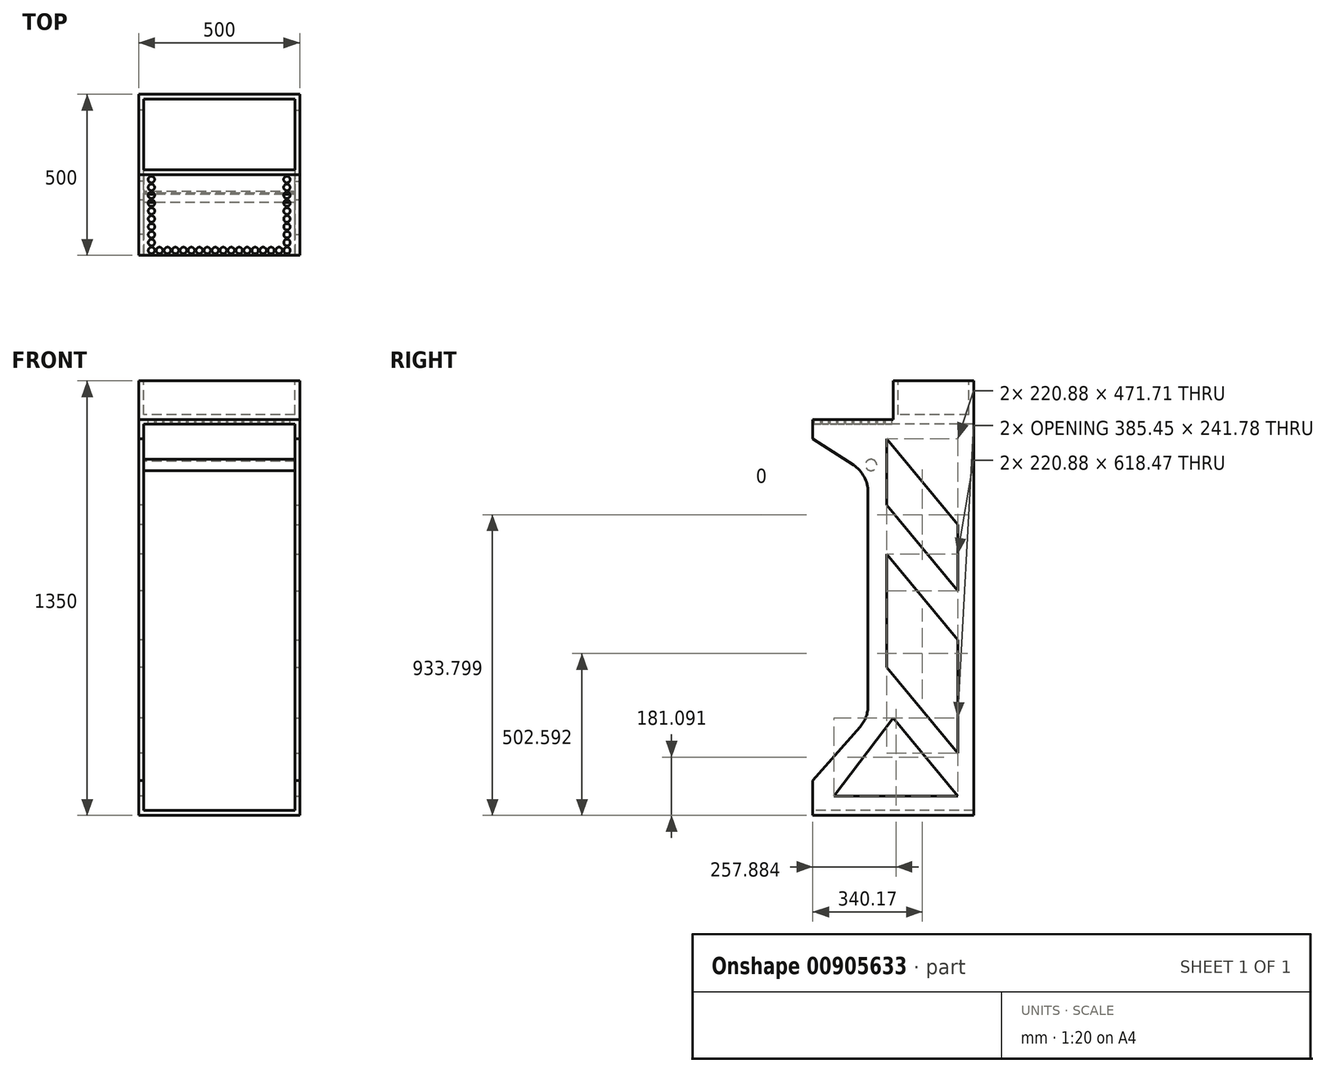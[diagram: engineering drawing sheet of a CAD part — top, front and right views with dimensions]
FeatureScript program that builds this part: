
annotation { "Feature Type Name" : "Feature", "Feature Type Description" : "" }
export const myFeature = defineFeature(function(context is Context, id is Id, definition is map)
    precondition{}
    {
        {
            var Q0;
            Q0=qCreatedBy(makeId("Top.planeOp"),FACE);
            var sketch = newSketch(context, id + "F0", { "sketchPlane" : qUnion([Q0])});
            skLineSegment(sketch, "E0.bottom", {"start": v(250, 250) * mm, "end": v(-250, 250) * mm});
            skLineSegment(sketch, "E0.top", {"start": v(250, -250) * mm, "end": v(-250, -250) * mm});
            skLineSegment(sketch, "E0.left", {"start": v(250, 250) * mm, "end": v(250, -250) * mm});
            skLineSegment(sketch, "E0.right", {"start": v(-250, 250) * mm, "end": v(-250, -250) * mm});
            skPoint(sketch, "E0.middle", {"position": v(0, 0) * mm});
            skSolve(sketch);
        }
        {
            var Q0;
            Q0 = qSketchRegion(id + "F0", true);
            extrude(context, id + "F1", {"entities" : qUnion([Q0]), "depth" : 15 * mm, "offsetDistance" : 25 * mm});
        }
        {
            var Q0;
            Q0=makeQuery(id+"F1.opExtrude","CAP_FACE",FACE,{"disambiguationData":[OSD([sQuery(id+"F0.wireOp",EDGE,"E0.bottom"),sQuery(id+"F0.wireOp",EDGE,"E0.top"),sQuery(id+"F0.wireOp",EDGE,"E0.left"),sQuery(id+"F0.wireOp",EDGE,"E0.right")])],"isStart":false});
            var sketch = newSketch(context, id + "F2", { "sketchPlane" : qUnion([Q0])});
            skLineSegment(sketch, "E1.bottom", {"start": v(-250, 250) * mm, "end": v(-235, 250) * mm});
            skLineSegment(sketch, "E1.top", {"start": v(-250, -250) * mm, "end": v(-235, -250) * mm});
            skLineSegment(sketch, "E1.left", {"start": v(-250, 250) * mm, "end": v(-250, -250) * mm});
            skLineSegment(sketch, "E1.right", {"start": v(-235, 250) * mm, "end": v(-235, -250) * mm});
            skLineSegment(sketch, "E2.bottom", {"start": v(250, 250) * mm, "end": v(235, 250) * mm});
            skLineSegment(sketch, "E2.top", {"start": v(250, -250) * mm, "end": v(235, -250) * mm});
            skLineSegment(sketch, "E2.left", {"start": v(250, 250) * mm, "end": v(250, -250) * mm});
            skLineSegment(sketch, "E2.right", {"start": v(235, 250) * mm, "end": v(235, -250) * mm});
            skSolve(sketch);
        }
        {
            var Q0;
            Q0=makeQuery(id+"F2.imprint","IMPRINT",FACE,{"disambiguationData":[TD([[makeQuery(id+"F2.imprint","IMPRINT",EDGE,{"derivedFrom":sQuery(id+"F2.wireOp",EDGE,"E1.bottom")}),1.0]])]});
            var Q1;
            Q1=makeQuery(id+"F2.imprint","IMPRINT",FACE,{"disambiguationData":[TD([[makeQuery(id+"F2.imprint","IMPRINT",EDGE,{"derivedFrom":sQuery(id+"F2.wireOp",EDGE,"E2.bottom")}),1.0]])]});
            extrude(context, id + "F3", {"entities" : qUnion([Q0, Q1]), "operationType" : NewBodyOperationType.ADD, "depth" : 1200 * mm, "offsetDistance" : 25 * mm});
        }
        {
            var Q0;
            Q0=makeQuery(id+"F3.boolean.opBoolean","MERGE",FACE,{"derivedFrom":[makeQuery(id+"F1.opExtrude","SWEPT_FACE",FACE,{"disambiguationData":[OSD([sQuery(id+"F0.wireOp",EDGE,"E0.right")])]}),makeQuery(id+"F3.opExtrude","SWEPT_FACE",FACE,{"disambiguationData":[OSD([sQuery(id+"F2.wireOp",EDGE,"E1.left")])]})]});
            var sketch = newSketch(context, id + "F4", { "sketchPlane" : qUnion([Q0])});
            skLineSegment(sketch, "E3", {"start": v(250, 1169.65) * mm, "end": v(124.16, 1088.19) * mm});
            skLineSegment(sketch, "E4", {"start": v(78.51, 1004.24) * mm, "end": v(78.51, 341.11) * mm});
            skLineSegment(sketch, "E5", {"start": v(103.4, 275.1) * mm, "end": v(250, 108.32) * mm});
            skPoint(sketch, "E6.visualSharp", {"position": v(78.51, 303.4) * mm});
            skArc(sketch, "E6.filletArc", {"start": v(78.51, 341.11) * mm, "mid": v(84.94, 305.83) * mm, "end": v(103.4, 275.1) * mm});
            skPoint(sketch, "E7.visualSharp", {"position": v(78.51, 1058.63) * mm});
            skArc(sketch, "E7.filletArc", {"start": v(124.16, 1088.19) * mm, "mid": v(90.66, 1052.02) * mm, "end": v(78.51, 1004.24) * mm});
            skSolve(sketch);
        }
        {
            var Q0;
            Q0 = qSketchRegion(id + "F4", true);
            var Q1;
            {var subQ1=sQuery(id+"F4.wireOp",EDGE,"E3");Q1=makeQuery(id+"F4.imprint","IMPRINT",FACE,{"disambiguationData":[TD([[makeQuery(id+"F4.imprint","IMPRINT",EDGE,{"derivedFrom":subQ1}),1.0]])]});}
            extrude(context, id + "F5", {"entities" : qUnion([Q0, Q1]), "operationType" : NewBodyOperationType.REMOVE, "oppositeDirection" : true, "depth" : 500 * mm, "offsetDistance" : 25 * mm});
        }
        {
            var Q0;
            Q0=makeQuery(id+"F3.opExtrude","CAP_FACE",FACE,{"disambiguationData":[OSD([sQuery(id+"F2.wireOp",EDGE,"E1.bottom"),sQuery(id+"F2.wireOp",EDGE,"E1.top"),sQuery(id+"F2.wireOp",EDGE,"E1.left"),sQuery(id+"F2.wireOp",EDGE,"E1.right")])],"isStart":false});
            var sketch = newSketch(context, id + "F6", { "sketchPlane" : qUnion([Q0])});
            skLineSegment(sketch, "E8.bottom", {"start": v(-250, 250) * mm, "end": v(250, 250) * mm});
            skLineSegment(sketch, "E8.top", {"start": v(-250, -250) * mm, "end": v(250, -250) * mm});
            skLineSegment(sketch, "E8.left", {"start": v(-250, 250) * mm, "end": v(-250, -250) * mm});
            skLineSegment(sketch, "E8.right", {"start": v(250, 250) * mm, "end": v(250, -250) * mm});
            skSolve(sketch);
        }
        {
            var Q0;
            Q0 = qSketchRegion(id + "F6", true);
            extrude(context, id + "F7", {"entities" : qUnion([Q0]), "operationType" : NewBodyOperationType.ADD, "depth" : 15 * mm, "offsetDistance" : 25 * mm});
        }
        {
            var Q0;
            Q0=makeQuery(id+"F7.opExtrude","CAP_FACE",FACE,{"disambiguationData":[OSD([sQuery(id+"F6.wireOp",EDGE,"E8.bottom"),sQuery(id+"F6.wireOp",EDGE,"E8.top"),sQuery(id+"F6.wireOp",EDGE,"E8.left"),sQuery(id+"F6.wireOp",EDGE,"E8.right")])],"isStart":false});
            var sketch = newSketch(context, id + "F8", { "sketchPlane" : qUnion([Q0])});
            skLineSegment(sketch, "E9", {"start": v(-250, 0) * mm, "end": v(250, 0) * mm});
            skLineSegment(sketch, "E10", {"start": v(250, 0) * mm, "end": v(250, 250) * mm});
            skLineSegment(sketch, "E11", {"start": v(250, 250) * mm, "end": v(-250, 250) * mm});
            skLineSegment(sketch, "E12", {"start": v(-250, 250) * mm, "end": v(-250, 0) * mm});
            skSolve(sketch);
        }
        {
            var Q0;
            Q0=makeQuery(id+"F8.imprint","IMPRINT",FACE,{"disambiguationData":[TD([[makeQuery(id+"F8.imprint","IMPRINT",EDGE,{"derivedFrom":sQuery(id+"F8.wireOp",EDGE,"E9")}),1.0]])]});
            extrude(context, id + "F9", {"entities" : qUnion([Q0]), "operationType" : NewBodyOperationType.ADD, "depth" : 120 * mm, "offsetDistance" : 25 * mm});
        }
        {
            var Q0;
            Q0=makeQuery(id+"F9.opExtrude","CAP_FACE",FACE,{"disambiguationData":[OSD([sQuery(id+"F8.wireOp",EDGE,"E9"),sQuery(id+"F8.wireOp",EDGE,"E10"),sQuery(id+"F8.wireOp",EDGE,"E11"),sQuery(id+"F8.wireOp",EDGE,"E12")])],"isStart":false});
            var sketch = newSketch(context, id + "F10", { "sketchPlane" : qUnion([Q0])});
            skLineSegment(sketch, "E13.0", {"start": v(-235, 235) * mm, "end": v(-235, 15) * mm});
            skLineSegment(sketch, "E13.1", {"start": v(235, 235) * mm, "end": v(-235, 235) * mm});
            skLineSegment(sketch, "E13.2", {"start": v(235, 15) * mm, "end": v(235, 235) * mm});
            skLineSegment(sketch, "E13.3", {"start": v(-235, 15) * mm, "end": v(235, 15) * mm});
            skSolve(sketch);
        }
        {
            var Q0;
            Q0=makeQuery(id+"F10.imprint","IMPRINT",FACE,{"disambiguationData":[TD([[makeQuery(id+"F10.imprint","IMPRINT",EDGE,{"derivedFrom":sQuery(id+"F10.wireOp",EDGE,"E13.0")}),1.0]])]});
            extrude(context, id + "F11", {"entities" : qUnion([Q0]), "operationType" : NewBodyOperationType.REMOVE, "oppositeDirection" : true, "depth" : 105 * mm, "offsetDistance" : 25 * mm});
        }
        {
            var Q0;
            Q0=makeQuery(id+"F7.opExtrude","CAP_FACE",FACE,{"disambiguationData":[OSD([sQuery(id+"F6.wireOp",EDGE,"E8.bottom"),sQuery(id+"F6.wireOp",EDGE,"E8.top"),sQuery(id+"F6.wireOp",EDGE,"E8.left"),sQuery(id+"F6.wireOp",EDGE,"E8.right")])],"isStart":false});
            var sketch = newSketch(context, id + "F12", { "sketchPlane" : qUnion([Q0])});
            skLineSegment(sketch, "E14", {"start": v(235, -250) * mm, "end": v(235, -235) * mm, "construction": true});
            skLineSegment(sketch, "E15", {"start": v(235, -235) * mm, "end": v(250, -235) * mm, "construction": true});
            skCircle(sketch, "E16.1.0.0", {"center": v(-210.25, -235) * mm, "radius": 10 * mm});
            skCircle(sketch, "E16.2.0.0", {"center": v(-185.5, -235) * mm, "radius": 10 * mm});
            skCircle(sketch, "E16.3.0.0", {"center": v(-160.75, -235) * mm, "radius": 10 * mm});
            skCircle(sketch, "E16.4.0.0", {"center": v(-136, -235) * mm, "radius": 10 * mm});
            skCircle(sketch, "E16.5.0.0", {"center": v(-111.25, -235) * mm, "radius": 10 * mm});
            skCircle(sketch, "E16.6.0.0", {"center": v(-86.5, -235) * mm, "radius": 10 * mm});
            skCircle(sketch, "E16.7.0.0", {"center": v(-61.75, -235) * mm, "radius": 10 * mm});
            skCircle(sketch, "E16.8.0.0", {"center": v(-37, -235) * mm, "radius": 10 * mm});
            skCircle(sketch, "E16.9.0.0", {"center": v(-12.25, -235) * mm, "radius": 10 * mm});
            skCircle(sketch, "E16.10.0.0", {"center": v(12.5, -235) * mm, "radius": 10 * mm});
            skCircle(sketch, "E16.11.0.0", {"center": v(37.25, -235) * mm, "radius": 10 * mm});
            skCircle(sketch, "E16.12.0.0", {"center": v(62, -235) * mm, "radius": 10 * mm});
            skCircle(sketch, "E16.13.0.0", {"center": v(86.75, -235) * mm, "radius": 10 * mm});
            skCircle(sketch, "E16.14.0.0", {"center": v(111.5, -235) * mm, "radius": 10 * mm});
            skCircle(sketch, "E16.15.0.0", {"center": v(136.25, -235) * mm, "radius": 10 * mm});
            skCircle(sketch, "E16.16.0.0", {"center": v(161, -235) * mm, "radius": 10 * mm});
            skCircle(sketch, "E16.17.0.0", {"center": v(185.75, -235) * mm, "radius": 10 * mm});
            skCircle(sketch, "E16.18.0.0", {"center": v(210.5, -235) * mm, "radius": 10 * mm});
            skLineSegment(sketch, "E17", {"start": v(235, -250) * mm, "end": v(235, 0) * mm, "construction": true});
            skLineSegment(sketch, "E18", {"start": v(250, -15) * mm, "end": v(235, -15) * mm, "construction": true});
            skLineSegment(sketch, "E19.direction1", {"start": v(235.25, -235) * mm, "end": v(260.25, -235) * mm, "construction": true});
            skCircle(sketch, "E20.0.1.0", {"center": v(-210.3, -210.5) * mm, "radius": 10 * mm});
            skCircle(sketch, "E20.0.2.0", {"center": v(-210.34, -186) * mm, "radius": 10 * mm});
            skCircle(sketch, "E20.0.3.0", {"center": v(-210.39, -161.5) * mm, "radius": 10 * mm});
            skCircle(sketch, "E20.0.4.0", {"center": v(-210.43, -137) * mm, "radius": 10 * mm});
            skCircle(sketch, "E20.0.5.0", {"center": v(-210.48, -112.5) * mm, "radius": 10 * mm});
            skCircle(sketch, "E20.0.6.0", {"center": v(-210.53, -88) * mm, "radius": 10 * mm});
            skCircle(sketch, "E20.0.7.0", {"center": v(-210.57, -63.5) * mm, "radius": 10 * mm});
            skCircle(sketch, "E20.0.8.0", {"center": v(-210.62, -39) * mm, "radius": 10 * mm});
            skCircle(sketch, "E20.0.9.0", {"center": v(-210.66, -14.5) * mm, "radius": 10 * mm});
            skLineSegment(sketch, "E20.direction2", {"start": v(-210.25, -235) * mm, "end": v(-210.3, -210.5) * mm, "construction": true});
            skCircle(sketch, "E21.0.1.0", {"center": v(210.45, -210.5) * mm, "radius": 10 * mm});
            skCircle(sketch, "E21.0.2.0", {"center": v(210.4, -186) * mm, "radius": 10 * mm});
            skCircle(sketch, "E21.0.3.0", {"center": v(210.36, -161.5) * mm, "radius": 10 * mm});
            skCircle(sketch, "E21.0.4.0", {"center": v(210.32, -137) * mm, "radius": 10 * mm});
            skCircle(sketch, "E21.0.5.0", {"center": v(210.27, -112.5) * mm, "radius": 10 * mm});
            skCircle(sketch, "E21.0.6.0", {"center": v(210.22, -88) * mm, "radius": 10 * mm});
            skCircle(sketch, "E21.0.7.0", {"center": v(210.18, -63.5) * mm, "radius": 10 * mm});
            skCircle(sketch, "E21.0.8.0", {"center": v(210.13, -39) * mm, "radius": 10 * mm});
            skCircle(sketch, "E21.0.9.0", {"center": v(210.09, -14.5) * mm, "radius": 10 * mm});
            skLineSegment(sketch, "E21.direction2", {"start": v(210.5, -235) * mm, "end": v(210.45, -210.5) * mm, "construction": true});
            skSolve(sketch);
        }
        {
            var Q0;
            Q0 = qSketchRegion(id + "F12", true);
            extrude(context, id + "F13", {"entities" : qUnion([Q0]), "operationType" : NewBodyOperationType.REMOVE, "oppositeDirection" : true, "depth" : 25 * mm, "offsetDistance" : 25 * mm});
        }
        {
            var Q0;
            Q0=makeQuery(id+"F9.boolean.opBoolean","MERGE",FACE,{"derivedFrom":[makeQuery(id+"F7.boolean.opBoolean","MERGE",FACE,{"derivedFrom":[makeQuery(id+"F3.boolean.opBoolean","MERGE",FACE,{"derivedFrom":[makeQuery(id+"F1.opExtrude","SWEPT_FACE",FACE,{"disambiguationData":[OSD([sQuery(id+"F0.wireOp",EDGE,"E0.right")])]}),makeQuery(id+"F3.opExtrude","SWEPT_FACE",FACE,{"disambiguationData":[OSD([sQuery(id+"F2.wireOp",EDGE,"E1.left")])]})]}),makeQuery(id+"F7.opExtrude","SWEPT_FACE",FACE,{"disambiguationData":[OSD([sQuery(id+"F6.wireOp",EDGE,"E8.left")])]})]}),makeQuery(id+"F9.opExtrude","SWEPT_FACE",FACE,{"disambiguationData":[OSD([sQuery(id+"F8.wireOp",EDGE,"E12")])]})]});
            var sketch = newSketch(context, id + "F14", { "sketchPlane" : qUnion([Q0])});
            skLineSegment(sketch, "E22", {"start": v(-200.6, 60.2) * mm, "end": v(184.84, 60.2) * mm});
            skLineSegment(sketch, "E23", {"start": v(184.84, 60.2) * mm, "end": v(0, 301.98) * mm});
            skLineSegment(sketch, "E24", {"start": v(0, 301.98) * mm, "end": v(-200.6, 60.2) * mm});
            skLineSegment(sketch, "E25", {"start": v(-200.6, 193.36) * mm, "end": v(20.27, 459.57) * mm});
            skLineSegment(sketch, "E26", {"start": v(20.27, 459.57) * mm, "end": v(20.27, 811.83) * mm});
            skLineSegment(sketch, "E27", {"start": v(20.27, 811.83) * mm, "end": v(-200.6, 545.62) * mm});
            skLineSegment(sketch, "E28", {"start": v(-200.6, 545.62) * mm, "end": v(-200.6, 193.36) * mm});
            skLineSegment(sketch, "E29", {"start": v(-200.6, 697.95) * mm, "end": v(20.27, 964.16) * mm});
            skLineSegment(sketch, "E30", {"start": v(20.27, 964.16) * mm, "end": v(20.27, 1169.65) * mm});
            skLineSegment(sketch, "E31", {"start": v(20.27, 1169.65) * mm, "end": v(-200.6, 903.44) * mm});
            skLineSegment(sketch, "E32", {"start": v(-200.6, 903.44) * mm, "end": v(-200.6, 697.95) * mm});
            skSolve(sketch);
        }
        {
            var Q0;
            Q0=makeQuery(id+"F14.imprint","IMPRINT",FACE,{"disambiguationData":[TD([[makeQuery(id+"F14.imprint","IMPRINT",EDGE,{"derivedFrom":sQuery(id+"F14.wireOp",EDGE,"E22")}),1.0]])]});
            var Q1;
            Q1=makeQuery(id+"F14.imprint","IMPRINT",FACE,{"disambiguationData":[TD([[makeQuery(id+"F14.imprint","IMPRINT",EDGE,{"derivedFrom":sQuery(id+"F14.wireOp",EDGE,"E25")}),1.0]])]});
            var Q2;
            Q2=makeQuery(id+"F14.imprint","IMPRINT",FACE,{"disambiguationData":[TD([[makeQuery(id+"F14.imprint","IMPRINT",EDGE,{"derivedFrom":sQuery(id+"F14.wireOp",EDGE,"E29")}),1.0]])]});
            extrude(context, id + "F15", {"entities" : qUnion([Q0, Q1, Q2]), "operationType" : NewBodyOperationType.REMOVE, "oppositeDirection" : true, "depth" : 25 * mm, "offsetDistance" : 25 * mm});
        }
        {
            var Q0;
            Q0=makeQuery(id+"F9.boolean.opBoolean","MERGE",FACE,{"derivedFrom":[makeQuery(id+"F7.boolean.opBoolean","MERGE",FACE,{"derivedFrom":[makeQuery(id+"F3.boolean.opBoolean","MERGE",FACE,{"derivedFrom":[makeQuery(id+"F1.opExtrude","SWEPT_FACE",FACE,{"disambiguationData":[OSD([sQuery(id+"F0.wireOp",EDGE,"E0.left")])]}),makeQuery(id+"F3.opExtrude","SWEPT_FACE",FACE,{"disambiguationData":[OSD([sQuery(id+"F2.wireOp",EDGE,"E2.left")])]})]}),makeQuery(id+"F7.opExtrude","SWEPT_FACE",FACE,{"disambiguationData":[OSD([sQuery(id+"F6.wireOp",EDGE,"E8.right")])]})]}),makeQuery(id+"F9.opExtrude","SWEPT_FACE",FACE,{"disambiguationData":[OSD([sQuery(id+"F8.wireOp",EDGE,"E10")])]})]});
            var sketch = newSketch(context, id + "F16", { "sketchPlane" : qUnion([Q0])});
            skLineSegment(sketch, "E33.0", {"start": v(-20.27, 1169.65) * mm, "end": v(200.6, 903.44) * mm});
            skLineSegment(sketch, "E33.1", {"start": v(-20.27, 964.16) * mm, "end": v(-20.27, 1169.65) * mm});
            skLineSegment(sketch, "E33.2", {"start": v(200.6, 697.95) * mm, "end": v(-20.27, 964.16) * mm});
            skLineSegment(sketch, "E33.3", {"start": v(200.6, 903.44) * mm, "end": v(200.6, 697.95) * mm});
            skLineSegment(sketch, "E34.0", {"start": v(-20.27, 811.83) * mm, "end": v(200.6, 545.62) * mm});
            skLineSegment(sketch, "E34.1", {"start": v(-20.27, 459.57) * mm, "end": v(-20.27, 811.83) * mm});
            skLineSegment(sketch, "E34.2", {"start": v(200.6, 193.36) * mm, "end": v(-20.27, 459.57) * mm});
            skLineSegment(sketch, "E34.3", {"start": v(200.6, 545.62) * mm, "end": v(200.6, 193.36) * mm});
            skLineSegment(sketch, "E35.0", {"start": v(0, 301.98) * mm, "end": v(200.6, 60.2) * mm});
            skLineSegment(sketch, "E35.1", {"start": v(-184.84, 60.2) * mm, "end": v(0, 301.98) * mm});
            skLineSegment(sketch, "E35.2", {"start": v(200.6, 60.2) * mm, "end": v(-184.84, 60.2) * mm});
            skSolve(sketch);
        }
        {
            var Q0;
            Q0 = qSketchRegion(id + "F16", true);
            extrude(context, id + "F17", {"entities" : qUnion([Q0]), "operationType" : NewBodyOperationType.REMOVE, "oppositeDirection" : true, "depth" : 25 * mm, "offsetDistance" : 25 * mm});
        }
        {
            var Q0;
            Q0=makeQuery(id+"F14.imprint","IMPRINT",FACE,{"disambiguationData":[TD([[makeQuery(id+"F14.imprint","IMPRINT",EDGE,{"derivedFrom":sQuery(id+"F14.wireOp",EDGE,"E22")}),-1.0]])]});
            var sketch = newSketch(context, id + "F18", { "sketchPlane" : qUnion([Q0])});
            skCircle(sketch, "E36", {"center": v(69.19, 1088.43) * mm, "radius": 17.5 * mm});
            skFitSpline(sketch, "E37", {"points": [v(81.78, 1076.28) * mm, v(82.63, 1077.22) * mm, v(84.02, 1079.14) * mm, v(85.16, 1081.3) * mm, v(87.66, 1083.56) * mm, v(134.5, 1095.02) * mm, v(142.25, 1091.6) * mm], "startDerivative": vector(9.84, 13.33) * mm, "endDerivative": vector(25, -26.82) * mm});
            skFitSpline(sketch, "E38", {"points": [v(53.92, 1096.98) * mm, v(56.46, 1100.44) * mm, v(60.34, 1103.53) * mm, v(63.65, 1105.03) * mm, v(73.86, 1109.46) * mm, v(118.75, 1120.2) * mm, v(165.3, 1114.94) * mm], "startDerivative": vector(28.64, 35.25) * mm, "endDerivative": vector(138.3, -27.6) * mm});
            skSolve(sketch);
        }
        {
            var Q0;
            Q0 = qSketchRegion(id + "F18", true);
            extrude(context, id + "F19", {"entities" : qUnion([Q0]), "operationType" : NewBodyOperationType.ADD, "oppositeDirection" : true, "depth" : 500 * mm, "offsetDistance" : 25 * mm});
        }
    });
